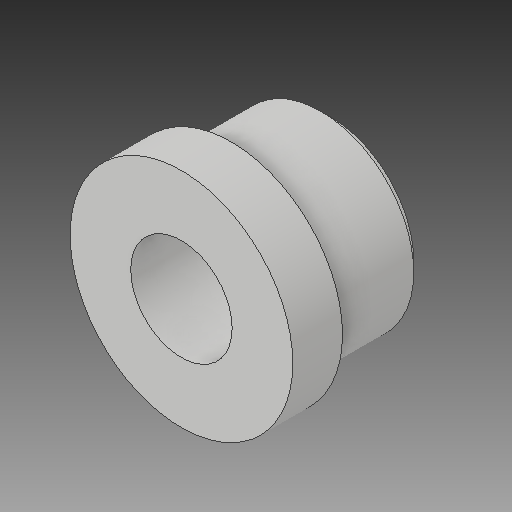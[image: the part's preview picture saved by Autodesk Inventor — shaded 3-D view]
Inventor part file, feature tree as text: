
AUTODESK INVENTOR PART (.ipt)
format: ipt  version: 2018 (Build 220112000, 112)  size: 110,080 bytes
history: native  units: in
note: dims shown in document units (in); Inventor stores cm internally (conversion verified against a paired STEP export)
features: revolve x1
ambient origin geometry x8: Origin, YZ Plane, XZ Plane, XY Plane, X Axis, Y Axis, Z Axis, Center Point
bodies: Solid1 (feature_tree)
feature tree (1):
  revolve  "Revolve1"  [1 undecoded]
note: 1 required parameter value undecoded (feature->parameter linkage not recoverable at this tier; creation-order binding heuristic only, values carry confidence <= 0.55)
